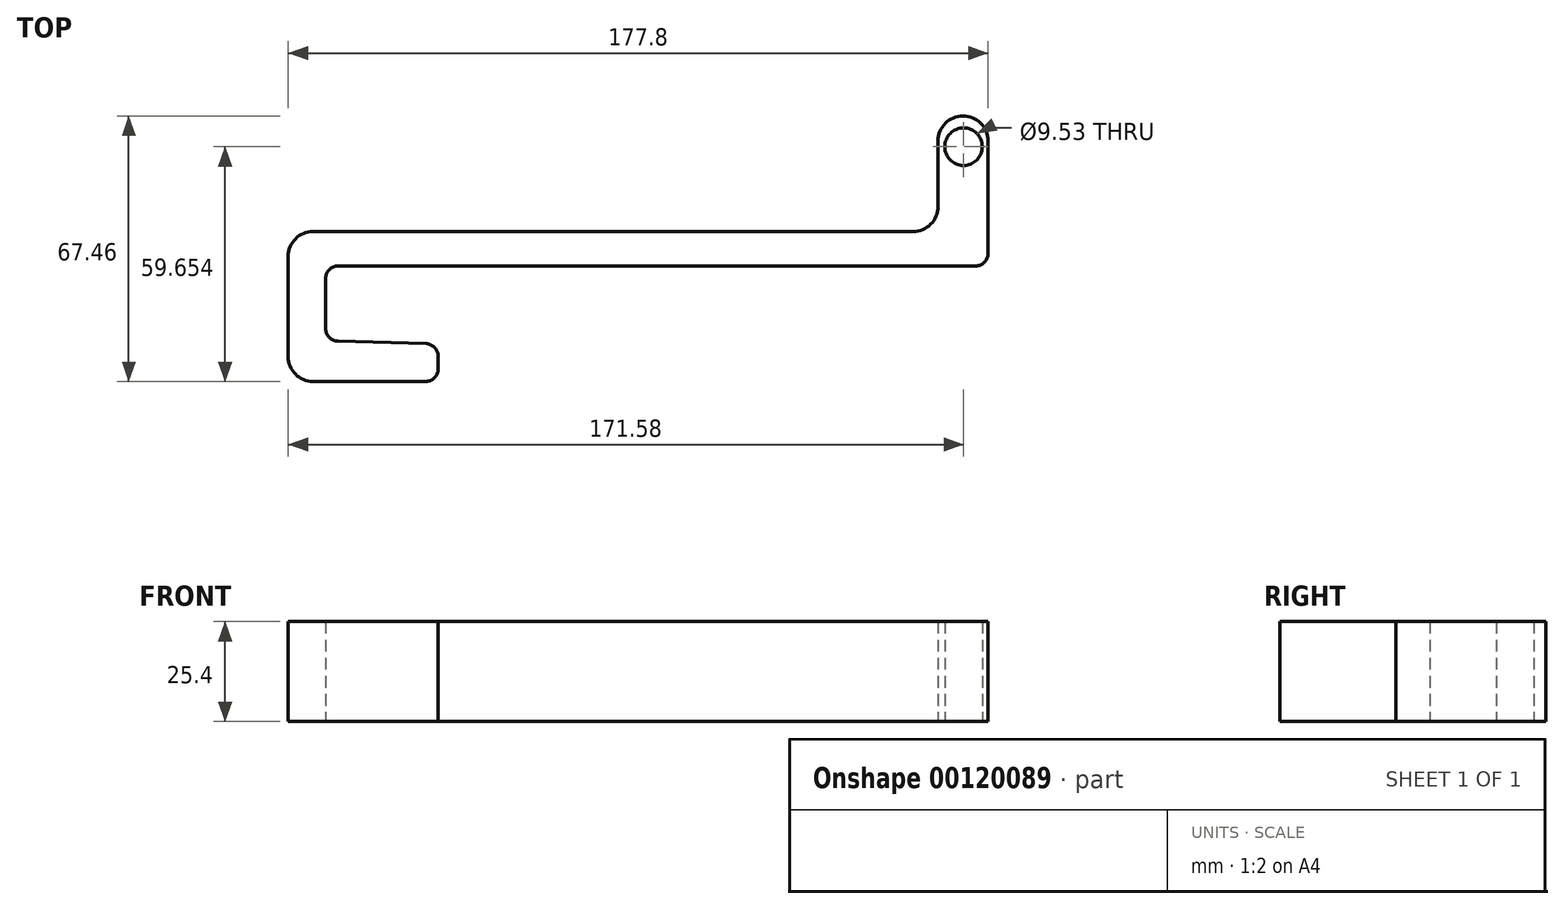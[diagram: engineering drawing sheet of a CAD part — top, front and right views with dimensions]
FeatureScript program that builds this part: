
annotation { "Feature Type Name" : "Feature", "Feature Type Description" : "" }
export const myFeature = defineFeature(function(context is Context, id is Id, definition is map)
    precondition{}
    {
        {
            var Q0;
            Q0=qCreatedBy(makeId("Right.planeOp"),FACE);
            var sketch = newSketch(context, id + "F0", { "sketchPlane" : qUnion([Q0])});
            skLineSegment(sketch, "E0", {"start": v(-17.14, 20.6) * mm, "end": v(-20.4, 20.6) * mm});
            skLineSegment(sketch, "E1", {"start": v(-23.58, 23.77) * mm, "end": v(-23.58, 52.35) * mm});
            skLineSegment(sketch, "E2", {"start": v(-17.23, 58.7) * mm, "end": v(8.17, 58.7) * mm});
            skLineSegment(sketch, "E3", {"start": v(14.52, 52.35) * mm, "end": v(14.52, -100.05) * mm});
            skLineSegment(sketch, "E4", {"start": v(20.87, -106.4) * mm, "end": v(37.53, -106.4) * mm});
            skLineSegment(sketch, "E5", {"start": v(43.88, -112.75) * mm, "end": v(43.88, -119.1) * mm, "construction": true});
            skLineSegment(sketch, "E6", {"start": v(37.53, -119.1) * mm, "end": v(8.95, -119.1) * mm});
            skLineSegment(sketch, "E7", {"start": v(5.78, -115.93) * mm, "end": v(5.78, 45.98) * mm});
            skLineSegment(sketch, "E8", {"start": v(2.6, 49.16) * mm, "end": v(-10.18, 49.16) * mm});
            skLineSegment(sketch, "E9", {"start": v(-13.36, 46.07) * mm, "end": v(-13.97, 23.68) * mm});
            skCircle(sketch, "E10", {"center": v(36.07, -112.88) * mm, "radius": 4.76 * mm});
            skPoint(sketch, "E11.visualSharp", {"position": v(-23.58, 58.7) * mm});
            skArc(sketch, "E11.filletArc", {"start": v(-17.23, 58.7) * mm, "mid": v(-21.72, 56.84) * mm, "end": v(-23.58, 52.35) * mm});
            skPoint(sketch, "E12.visualSharp", {"position": v(14.52, 58.7) * mm});
            skArc(sketch, "E12.filletArc", {"start": v(14.52, 52.35) * mm, "mid": v(12.66, 56.84) * mm, "end": v(8.17, 58.7) * mm});
            skPoint(sketch, "E13.visualSharp", {"position": v(-23.58, 20.6) * mm});
            skArc(sketch, "E13.filletArc", {"start": v(-23.58, 23.77) * mm, "mid": v(-22.65, 21.53) * mm, "end": v(-20.4, 20.6) * mm});
            skPoint(sketch, "E14.visualSharp", {"position": v(5.78, -119.1) * mm});
            skArc(sketch, "E14.filletArc", {"start": v(5.78, -115.93) * mm, "mid": v(6.7, -118.17) * mm, "end": v(8.95, -119.1) * mm});
            skPoint(sketch, "E15.visualSharp", {"position": v(14.52, -106.4) * mm});
            skArc(sketch, "E15.filletArc", {"start": v(14.52, -100.05) * mm, "mid": v(16.38, -104.54) * mm, "end": v(20.87, -106.4) * mm});
            skPoint(sketch, "E16.visualSharp", {"position": v(-13.27, 49.16) * mm});
            skArc(sketch, "E16.filletArc", {"start": v(-10.18, 49.16) * mm, "mid": v(-12.4, 48.26) * mm, "end": v(-13.36, 46.07) * mm});
            skPoint(sketch, "E17.visualSharp", {"position": v(5.78, 49.16) * mm});
            skArc(sketch, "E17.filletArc", {"start": v(5.78, 45.98) * mm, "mid": v(4.85, 48.23) * mm, "end": v(2.6, 49.16) * mm});
            skPoint(sketch, "E18.visualSharp", {"position": v(-14.05, 20.6) * mm});
            skArc(sketch, "E18.filletArc", {"start": v(-17.14, 20.6) * mm, "mid": v(-14.93, 21.5) * mm, "end": v(-13.97, 23.68) * mm});
            skPoint(sketch, "E19.visualSharp", {"position": v(43.88, -106.4) * mm});
            skArc(sketch, "E19.filletArc", {"start": v(43.88, -112.75) * mm, "mid": v(42.02, -108.26) * mm, "end": v(37.53, -106.4) * mm});
            skLineSegment(sketch, "E20", {"start": v(43.88, -119.1) * mm, "end": v(43.88, -112.75) * mm, "construction": true});
            skLineSegment(sketch, "E21", {"start": v(43.88, -112.75) * mm, "end": v(43.88, -112.75) * mm});
            skPoint(sketch, "E22.visualSharp", {"position": v(43.88, -119.1) * mm});
            skArc(sketch, "E22.filletArc", {"start": v(37.53, -119.1) * mm, "mid": v(42.02, -117.24) * mm, "end": v(43.88, -112.75) * mm});
            skSolve(sketch);
        }
        {
            var Q0;
            Q0=makeQuery(id+"F0.imprint","IMPRINT",FACE,{"disambiguationData":[TD([[makeQuery(id+"F0.imprint","IMPRINT",EDGE,{"derivedFrom":sQuery(id+"F0.wireOp",EDGE,"E0")}),-1.0]])]});
            extrude(context, id + "F1", {"entities" : qUnion([Q0]), "depth" : 25.4 * mm});
        }
        {
            var Q0;
            Q0=makeQuery(id+"F1.opExtrude","SWEPT_BODY",BODY,{"disambiguationData":[OSD([sQuery(id+"F0.wireOp",EDGE,"E0"),sQuery(id+"F0.wireOp",EDGE,"E1"),sQuery(id+"F0.wireOp",EDGE,"E2"),sQuery(id+"F0.wireOp",EDGE,"E3"),sQuery(id+"F0.wireOp",EDGE,"E4"),sQuery(id+"F0.wireOp",EDGE,"E6"),sQuery(id+"F0.wireOp",EDGE,"E7"),sQuery(id+"F0.wireOp",EDGE,"E8"),sQuery(id+"F0.wireOp",EDGE,"E9"),sQuery(id+"F0.wireOp",EDGE,"E10"),sQuery(id+"F0.wireOp",EDGE,"E11.filletArc"),sQuery(id+"F0.wireOp",EDGE,"E12.filletArc"),sQuery(id+"F0.wireOp",EDGE,"E13.filletArc"),sQuery(id+"F0.wireOp",EDGE,"E14.filletArc"),sQuery(id+"F0.wireOp",EDGE,"E15.filletArc"),sQuery(id+"F0.wireOp",EDGE,"E16.filletArc"),sQuery(id+"F0.wireOp",EDGE,"E17.filletArc"),sQuery(id+"F0.wireOp",EDGE,"E18.filletArc"),sQuery(id+"F0.wireOp",EDGE,"E19.filletArc"),sQuery(id+"F0.wireOp",EDGE,"E22.filletArc")])]});
            var Q1;
            Q1=makeQuery(id+"F1.opExtrude","CAP_EDGE",EDGE,{"disambiguationData":[OSD([sQuery(id+"F0.wireOp",EDGE,"E6")])],"isStart":false});
            transform(context, id + "F2", {"entities" : qUnion([Q0]), "transformType" : TransformType.ROTATION, "transformAxis" : qUnion([Q1]), "angle" : 90 * degree, "makeCopy" : false});
        }
    });
